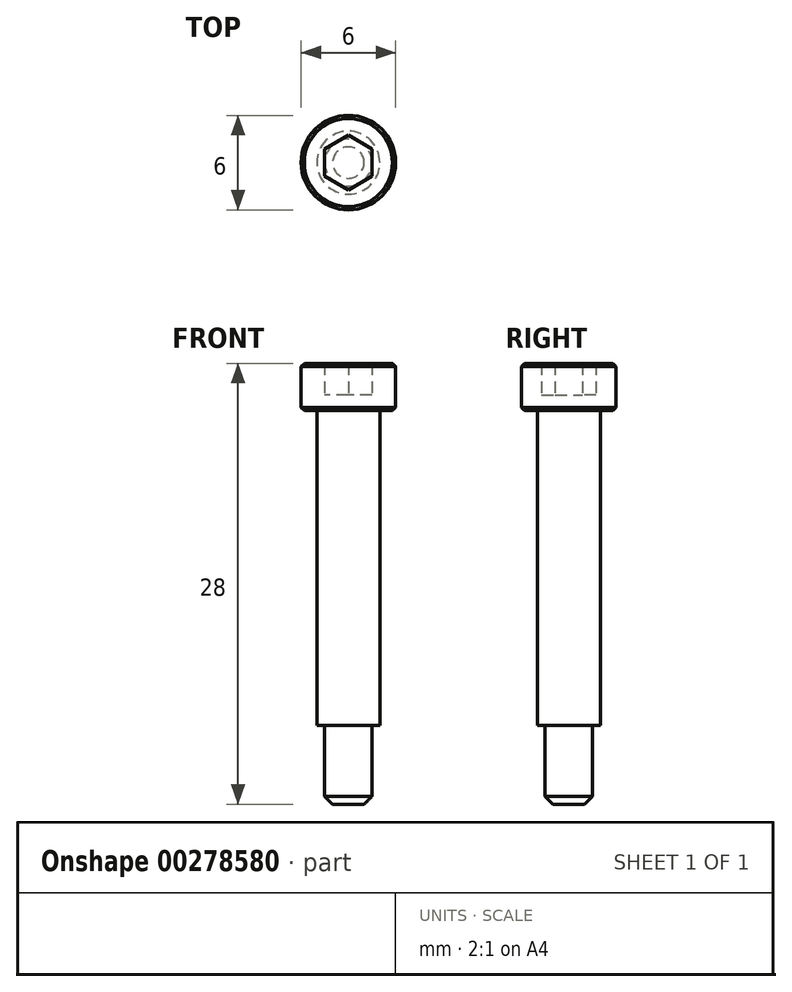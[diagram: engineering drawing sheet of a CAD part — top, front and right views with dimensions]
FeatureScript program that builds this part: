
annotation { "Feature Type Name" : "Feature", "Feature Type Description" : "" }
export const myFeature = defineFeature(function(context is Context, id is Id, definition is map)
    precondition{}
    {
        {
            var Q0;
            Q0=qCreatedBy(makeId("Top.planeOp"),FACE);
            var sketch = newSketch(context, id + "F0", { "sketchPlane" : qUnion([Q0])});
            skCircle(sketch, "E0", {"center": v(0, 0) * mm, "radius": 1.5 * mm});
            skCircle(sketch, "E1", {"center": v(0, 0) * mm, "radius": 2 * mm});
            skCircle(sketch, "E2", {"center": v(0, 0) * mm, "radius": 3 * mm});
            skCircle(sketch, "E3.cCircle", {"center": v(0, 0) * mm, "radius": 1.5 * mm, "construction": true});
            skLineSegment(sketch, "E3.0", {"start": v(1.5, 0.87) * mm, "end": v(1.5, -0.87) * mm});
            skLineSegment(sketch, "E3.1", {"start": v(1.5, -0.87) * mm, "end": v(0, -1.73) * mm});
            skLineSegment(sketch, "E3.2", {"start": v(0, -1.73) * mm, "end": v(-1.5, -0.87) * mm});
            skLineSegment(sketch, "E3.3", {"start": v(-1.5, -0.87) * mm, "end": v(-1.5, 0.87) * mm});
            skLineSegment(sketch, "E3.4", {"start": v(-1.5, 0.87) * mm, "end": v(0, 1.73) * mm});
            skLineSegment(sketch, "E3.5", {"start": v(0, 1.73) * mm, "end": v(1.5, 0.87) * mm});
            skPoint(sketch, "E3.0.midPoint", {"position": v(1.5, 0) * mm});
            skSolve(sketch);
        }
        {
            var Q0;
            Q0=makeQuery(id+"F0.imprint","IMPRINT",FACE,{"disambiguationData":[TD([[makeQuery(id+"F0.imprint","IMPRINT",EDGE,{"derivedFrom":sQuery(id+"F0.wireOp",EDGE,"E1")}),-1.0]])]});
            var Q1;
            {var subQ0=sQuery(id+"F0.wireOp",EDGE,"E0");var subQ4=makeQuery(id+"F0.imprint","INTERSECT",VERTEX,{"derivedFrom":[subQ0,sQuery(id+"F0.wireOp",EDGE,"E3.5")]});Q1=makeQuery(id+"F0.imprint","IMPRINT",FACE,{"disambiguationData":[TD([[makeQuery(id+"F0.imprint","IMPRINT",EDGE,{"disambiguationData":[TD([[subQ4,1.0]])],"derivedFrom":subQ0}),1.0]])]});}
            var Q2;
            {var subQ0=sQuery(id+"F0.wireOp",EDGE,"E3.2");var subQ1=sQuery(id+"F0.wireOp",EDGE,"E0");var subQ2=makeQuery(id+"F0.imprint","INTERSECT",VERTEX,{"derivedFrom":[subQ1,subQ0]});Q2=makeQuery(id+"F0.imprint","IMPRINT",FACE,{"disambiguationData":[TD([[makeQuery(id+"F0.imprint","IMPRINT",EDGE,{"disambiguationData":[TD([[subQ2,-1.0]])],"derivedFrom":subQ1}),-1.0]])]});}
            var Q3;
            {var subQ0=sQuery(id+"F0.wireOp",EDGE,"E3.0");var subQ1=sQuery(id+"F0.wireOp",EDGE,"E0");var subQ2=makeQuery(id+"F0.imprint","INTERSECT",VERTEX,{"derivedFrom":[subQ1,subQ0]});Q3=makeQuery(id+"F0.imprint","IMPRINT",FACE,{"disambiguationData":[TD([[makeQuery(id+"F0.imprint","IMPRINT",EDGE,{"disambiguationData":[TD([[subQ2,1.0]])],"derivedFrom":subQ1}),-1.0]])]});}
            var Q4;
            {var subQ0=sQuery(id+"F0.wireOp",EDGE,"E3.5");var subQ1=sQuery(id+"F0.wireOp",EDGE,"E0");var subQ2=makeQuery(id+"F0.imprint","INTERSECT",VERTEX,{"derivedFrom":[subQ1,subQ0]});Q4=makeQuery(id+"F0.imprint","IMPRINT",FACE,{"disambiguationData":[TD([[makeQuery(id+"F0.imprint","IMPRINT",EDGE,{"disambiguationData":[TD([[subQ2,1.0]])],"derivedFrom":subQ1}),-1.0]])]});}
            var Q5;
            {var subQ0=sQuery(id+"F0.wireOp",EDGE,"E3.5");var subQ1=sQuery(id+"F0.wireOp",EDGE,"E0");var subQ2=makeQuery(id+"F0.imprint","INTERSECT",VERTEX,{"derivedFrom":[subQ1,subQ0]});Q5=makeQuery(id+"F0.imprint","IMPRINT",FACE,{"disambiguationData":[TD([[makeQuery(id+"F0.imprint","IMPRINT",EDGE,{"disambiguationData":[TD([[subQ2,-1.0]])],"derivedFrom":subQ1}),-1.0]])]});}
            var Q6;
            {var subQ0=sQuery(id+"F0.wireOp",EDGE,"E3.4");var subQ1=sQuery(id+"F0.wireOp",EDGE,"E0");var subQ2=makeQuery(id+"F0.imprint","INTERSECT",VERTEX,{"derivedFrom":[subQ1,subQ0]});Q6=makeQuery(id+"F0.imprint","IMPRINT",FACE,{"disambiguationData":[TD([[makeQuery(id+"F0.imprint","IMPRINT",EDGE,{"disambiguationData":[TD([[subQ2,-1.0]])],"derivedFrom":subQ1}),-1.0]])]});}
            var Q7;
            {var subQ0=sQuery(id+"F0.wireOp",EDGE,"E3.3");var subQ1=sQuery(id+"F0.wireOp",EDGE,"E0");var subQ2=makeQuery(id+"F0.imprint","INTERSECT",VERTEX,{"derivedFrom":[subQ1,subQ0]});Q7=makeQuery(id+"F0.imprint","IMPRINT",FACE,{"disambiguationData":[TD([[makeQuery(id+"F0.imprint","IMPRINT",EDGE,{"disambiguationData":[TD([[subQ2,-1.0]])],"derivedFrom":subQ1}),-1.0]])]});}
            var Q8;
            Q8=makeQuery(id+"F0.imprint","IMPRINT",FACE,{"disambiguationData":[TD([[makeQuery(id+"F0.imprint","IMPRINT",EDGE,{"derivedFrom":sQuery(id+"F0.wireOp",EDGE,"E1")}),1.0]])]});
            extrude(context, id + "F1", {"entities" : qUnion([Q0, Q1, Q2, Q3, Q4, Q5, Q6, Q7, Q8]), "depth" : 3 * mm});
        }
        {
            var Q0;
            {var subQ0=sQuery(id+"F0.wireOp",EDGE,"E0");var subQ4=makeQuery(id+"F0.imprint","INTERSECT",VERTEX,{"derivedFrom":[subQ0,sQuery(id+"F0.wireOp",EDGE,"E3.5")]});Q0=makeQuery(id+"F0.imprint","IMPRINT",FACE,{"disambiguationData":[TD([[makeQuery(id+"F0.imprint","IMPRINT",EDGE,{"disambiguationData":[TD([[subQ4,1.0]])],"derivedFrom":subQ0}),1.0]])]});}
            var Q1;
            Q1=makeQuery(id+"F0.imprint","IMPRINT",FACE,{"disambiguationData":[TD([[makeQuery(id+"F0.imprint","IMPRINT",EDGE,{"derivedFrom":sQuery(id+"F0.wireOp",EDGE,"E1")}),1.0]])]});
            var Q2;
            {var subQ0=sQuery(id+"F0.wireOp",EDGE,"E3.2");var subQ1=sQuery(id+"F0.wireOp",EDGE,"E0");var subQ2=makeQuery(id+"F0.imprint","INTERSECT",VERTEX,{"derivedFrom":[subQ1,subQ0]});Q2=makeQuery(id+"F0.imprint","IMPRINT",FACE,{"disambiguationData":[TD([[makeQuery(id+"F0.imprint","IMPRINT",EDGE,{"disambiguationData":[TD([[subQ2,-1.0]])],"derivedFrom":subQ1}),-1.0]])]});}
            var Q3;
            {var subQ0=sQuery(id+"F0.wireOp",EDGE,"E3.0");var subQ1=sQuery(id+"F0.wireOp",EDGE,"E0");var subQ2=makeQuery(id+"F0.imprint","INTERSECT",VERTEX,{"derivedFrom":[subQ1,subQ0]});Q3=makeQuery(id+"F0.imprint","IMPRINT",FACE,{"disambiguationData":[TD([[makeQuery(id+"F0.imprint","IMPRINT",EDGE,{"disambiguationData":[TD([[subQ2,1.0]])],"derivedFrom":subQ1}),-1.0]])]});}
            var Q4;
            {var subQ0=sQuery(id+"F0.wireOp",EDGE,"E3.5");var subQ1=sQuery(id+"F0.wireOp",EDGE,"E0");var subQ2=makeQuery(id+"F0.imprint","INTERSECT",VERTEX,{"derivedFrom":[subQ1,subQ0]});Q4=makeQuery(id+"F0.imprint","IMPRINT",FACE,{"disambiguationData":[TD([[makeQuery(id+"F0.imprint","IMPRINT",EDGE,{"disambiguationData":[TD([[subQ2,1.0]])],"derivedFrom":subQ1}),-1.0]])]});}
            var Q5;
            {var subQ0=sQuery(id+"F0.wireOp",EDGE,"E3.5");var subQ1=sQuery(id+"F0.wireOp",EDGE,"E0");var subQ2=makeQuery(id+"F0.imprint","INTERSECT",VERTEX,{"derivedFrom":[subQ1,subQ0]});Q5=makeQuery(id+"F0.imprint","IMPRINT",FACE,{"disambiguationData":[TD([[makeQuery(id+"F0.imprint","IMPRINT",EDGE,{"disambiguationData":[TD([[subQ2,-1.0]])],"derivedFrom":subQ1}),-1.0]])]});}
            var Q6;
            {var subQ0=sQuery(id+"F0.wireOp",EDGE,"E3.4");var subQ1=sQuery(id+"F0.wireOp",EDGE,"E0");var subQ2=makeQuery(id+"F0.imprint","INTERSECT",VERTEX,{"derivedFrom":[subQ1,subQ0]});Q6=makeQuery(id+"F0.imprint","IMPRINT",FACE,{"disambiguationData":[TD([[makeQuery(id+"F0.imprint","IMPRINT",EDGE,{"disambiguationData":[TD([[subQ2,-1.0]])],"derivedFrom":subQ1}),-1.0]])]});}
            var Q7;
            {var subQ0=sQuery(id+"F0.wireOp",EDGE,"E3.3");var subQ1=sQuery(id+"F0.wireOp",EDGE,"E0");var subQ2=makeQuery(id+"F0.imprint","INTERSECT",VERTEX,{"derivedFrom":[subQ1,subQ0]});Q7=makeQuery(id+"F0.imprint","IMPRINT",FACE,{"disambiguationData":[TD([[makeQuery(id+"F0.imprint","IMPRINT",EDGE,{"disambiguationData":[TD([[subQ2,-1.0]])],"derivedFrom":subQ1}),-1.0]])]});}
            extrude(context, id + "F2", {"entities" : qUnion([Q0, Q1, Q2, Q3, Q4, Q5, Q6, Q7]), "operationType" : NewBodyOperationType.ADD, "oppositeDirection" : true, "depth" : 20 * mm});
        }
        {
            var Q0;
            {var subQ0=sQuery(id+"F0.wireOp",EDGE,"E0");var subQ4=makeQuery(id+"F0.imprint","INTERSECT",VERTEX,{"derivedFrom":[subQ0,sQuery(id+"F0.wireOp",EDGE,"E3.5")]});Q0=makeQuery(id+"F0.imprint","IMPRINT",FACE,{"disambiguationData":[TD([[makeQuery(id+"F0.imprint","IMPRINT",EDGE,{"disambiguationData":[TD([[subQ4,1.0]])],"derivedFrom":subQ0}),1.0]])]});}
            extrude(context, id + "F3", {"entities" : qUnion([Q0]), "operationType" : NewBodyOperationType.ADD, "oppositeDirection" : true, "depth" : 25 * mm});
        }
        {
            var Q0;
            {var subQ0=sQuery(id+"F0.wireOp",EDGE,"E0");var subQ4=makeQuery(id+"F0.imprint","INTERSECT",VERTEX,{"derivedFrom":[subQ0,sQuery(id+"F0.wireOp",EDGE,"E3.5")]});Q0=makeQuery(id+"F0.imprint","IMPRINT",FACE,{"disambiguationData":[TD([[makeQuery(id+"F0.imprint","IMPRINT",EDGE,{"disambiguationData":[TD([[subQ4,1.0]])],"derivedFrom":subQ0}),1.0]])]});}
            var Q1;
            {var subQ0=sQuery(id+"F0.wireOp",EDGE,"E3.5");var subQ1=sQuery(id+"F0.wireOp",EDGE,"E0");var subQ2=makeQuery(id+"F0.imprint","INTERSECT",VERTEX,{"derivedFrom":[subQ1,subQ0]});Q1=makeQuery(id+"F0.imprint","IMPRINT",FACE,{"disambiguationData":[TD([[makeQuery(id+"F0.imprint","IMPRINT",EDGE,{"disambiguationData":[TD([[subQ2,-1.0]])],"derivedFrom":subQ1}),-1.0]])]});}
            var Q2;
            {var subQ0=sQuery(id+"F0.wireOp",EDGE,"E3.5");var subQ1=sQuery(id+"F0.wireOp",EDGE,"E0");var subQ2=makeQuery(id+"F0.imprint","INTERSECT",VERTEX,{"derivedFrom":[subQ1,subQ0]});Q2=makeQuery(id+"F0.imprint","IMPRINT",FACE,{"disambiguationData":[TD([[makeQuery(id+"F0.imprint","IMPRINT",EDGE,{"disambiguationData":[TD([[subQ2,1.0]])],"derivedFrom":subQ1}),-1.0]])]});}
            var Q3;
            {var subQ0=sQuery(id+"F0.wireOp",EDGE,"E3.0");var subQ1=sQuery(id+"F0.wireOp",EDGE,"E0");var subQ2=makeQuery(id+"F0.imprint","INTERSECT",VERTEX,{"derivedFrom":[subQ1,subQ0]});Q3=makeQuery(id+"F0.imprint","IMPRINT",FACE,{"disambiguationData":[TD([[makeQuery(id+"F0.imprint","IMPRINT",EDGE,{"disambiguationData":[TD([[subQ2,1.0]])],"derivedFrom":subQ1}),-1.0]])]});}
            var Q4;
            {var subQ0=sQuery(id+"F0.wireOp",EDGE,"E3.2");var subQ1=sQuery(id+"F0.wireOp",EDGE,"E0");var subQ2=makeQuery(id+"F0.imprint","INTERSECT",VERTEX,{"derivedFrom":[subQ1,subQ0]});Q4=makeQuery(id+"F0.imprint","IMPRINT",FACE,{"disambiguationData":[TD([[makeQuery(id+"F0.imprint","IMPRINT",EDGE,{"disambiguationData":[TD([[subQ2,-1.0]])],"derivedFrom":subQ1}),-1.0]])]});}
            var Q5;
            {var subQ0=sQuery(id+"F0.wireOp",EDGE,"E3.4");var subQ1=sQuery(id+"F0.wireOp",EDGE,"E0");var subQ2=makeQuery(id+"F0.imprint","INTERSECT",VERTEX,{"derivedFrom":[subQ1,subQ0]});Q5=makeQuery(id+"F0.imprint","IMPRINT",FACE,{"disambiguationData":[TD([[makeQuery(id+"F0.imprint","IMPRINT",EDGE,{"disambiguationData":[TD([[subQ2,-1.0]])],"derivedFrom":subQ1}),-1.0]])]});}
            var Q6;
            {var subQ0=sQuery(id+"F0.wireOp",EDGE,"E3.3");var subQ1=sQuery(id+"F0.wireOp",EDGE,"E0");var subQ2=makeQuery(id+"F0.imprint","INTERSECT",VERTEX,{"derivedFrom":[subQ1,subQ0]});Q6=makeQuery(id+"F0.imprint","IMPRINT",FACE,{"disambiguationData":[TD([[makeQuery(id+"F0.imprint","IMPRINT",EDGE,{"disambiguationData":[TD([[subQ2,-1.0]])],"derivedFrom":subQ1}),-1.0]])]});}
            extrude(context, id + "F4", {"entities" : qUnion([Q0, Q1, Q2, Q3, Q4, Q5, Q6]), "operationType" : NewBodyOperationType.REMOVE, "depth" : 3 * mm, "hasSecondDirection" : true, "secondDirectionOppositeDirection" : false, "secondDirectionDepth" : 1 * mm});
        }
        {
            var Q0;
            Q0=makeQuery(id+"F1.opExtrude","CAP_EDGE",EDGE,{"disambiguationData":[OSD([sQuery(id+"F0.wireOp",EDGE,"E2")])],"isStart":false});
            var Q1;
            Q1=makeQuery(id+"F4.boolean.opBoolean","COPY",EDGE,{"derivedFrom":makeQuery(id+"F4.opExtrude","CAP_EDGE",EDGE,{"disambiguationData":[OSD([sQuery(id+"F0.wireOp",EDGE,"E3.4")])],"isStart":false})});
            var Q2;
            Q2=makeQuery(id+"F4.boolean.opBoolean","COPY",EDGE,{"derivedFrom":makeQuery(id+"F4.opExtrude","CAP_EDGE",EDGE,{"disambiguationData":[OSD([sQuery(id+"F0.wireOp",EDGE,"E3.5")])],"isStart":false})});
            var Q3;
            Q3=makeQuery(id+"F4.boolean.opBoolean","COPY",EDGE,{"derivedFrom":makeQuery(id+"F4.opExtrude","CAP_EDGE",EDGE,{"disambiguationData":[OSD([sQuery(id+"F0.wireOp",EDGE,"E3.0")])],"isStart":false})});
            var Q4;
            Q4=makeQuery(id+"F4.boolean.opBoolean","COPY",EDGE,{"derivedFrom":makeQuery(id+"F4.opExtrude","CAP_EDGE",EDGE,{"disambiguationData":[OSD([sQuery(id+"F0.wireOp",EDGE,"E3.1")])],"isStart":false})});
            var Q5;
            Q5=makeQuery(id+"F4.boolean.opBoolean","COPY",EDGE,{"derivedFrom":makeQuery(id+"F4.opExtrude","CAP_EDGE",EDGE,{"disambiguationData":[OSD([sQuery(id+"F0.wireOp",EDGE,"E3.3")])],"isStart":false})});
            var Q6;
            Q6=makeQuery(id+"F4.boolean.opBoolean","COPY",EDGE,{"derivedFrom":makeQuery(id+"F4.opExtrude","CAP_EDGE",EDGE,{"disambiguationData":[OSD([sQuery(id+"F0.wireOp",EDGE,"E3.2")])],"isStart":false})});
            var Q7;
            Q7=makeQuery(id+"F1.opExtrude","CAP_EDGE",EDGE,{"disambiguationData":[OSD([sQuery(id+"F0.wireOp",EDGE,"E2")])],"isStart":true});
            chamfer(context, id + "F5", {"entities" : qUnion([Q0, Q1, Q2, Q3, Q4, Q5, Q6, Q7]), "width" : 0.2 * mm, "tangentPropagation" : true});
        }
        {
            var Q0;
            Q0=makeQuery(id+"F3.opExtrude","CAP_EDGE",EDGE,{"disambiguationData":[OSD([sQuery(id+"F0.wireOp",EDGE,"E0")])],"isStart":false});
            chamfer(context, id + "F6", {"entities" : qUnion([Q0]), "width" : 0.5 * mm, "tangentPropagation" : true});
        }
    });
